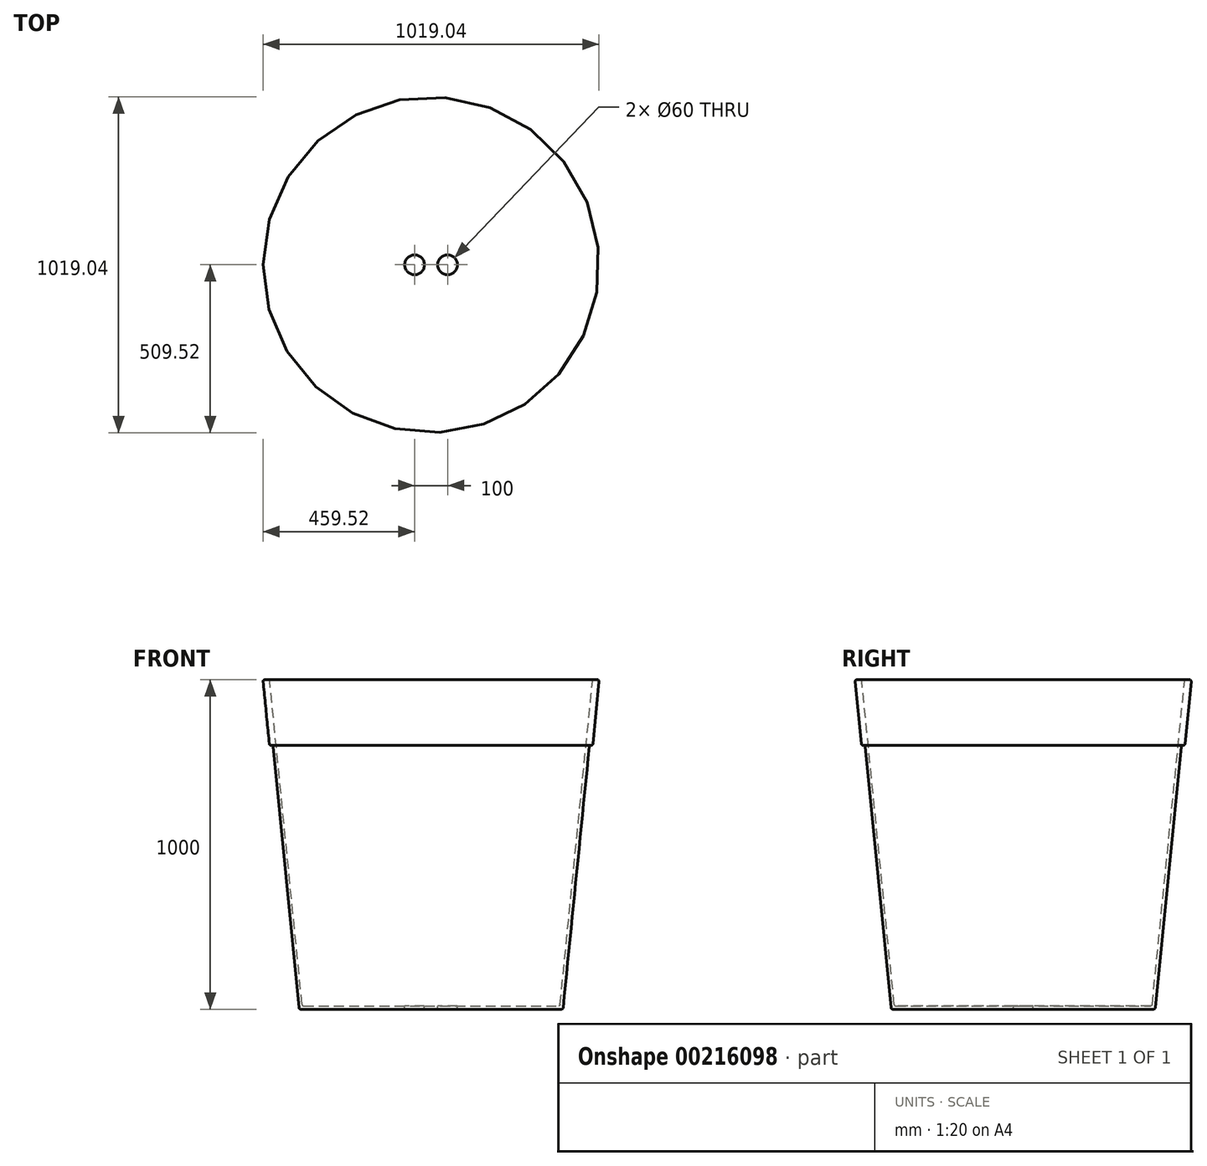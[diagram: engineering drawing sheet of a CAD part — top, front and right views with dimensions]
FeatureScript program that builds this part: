
annotation { "Feature Type Name" : "Feature", "Feature Type Description" : "" }
export const myFeature = defineFeature(function(context is Context, id is Id, definition is map)
    precondition{}
    {
        {
            var Q0;
            Q0=qCreatedBy(makeId("Front.planeOp"),FACE);
            var sketch = newSketch(context, id + "F0", { "sketchPlane" : qUnion([Q0])});
            skLineSegment(sketch, "E0", {"start": v(-400, 0) * mm, "end": v(-500, 1000) * mm});
            skLineSegment(sketch, "E1", {"start": v(-400, 0) * mm, "end": v(0, 0) * mm});
            skLineSegment(sketch, "E2", {"start": v(0, 0) * mm, "end": v(0, 10) * mm});
            skLineSegment(sketch, "E3", {"start": v(0, 10) * mm, "end": v(-390.95, 10) * mm});
            skLineSegment(sketch, "E4", {"start": v(-390.95, 10) * mm, "end": v(-489.95, 1000) * mm});
            skLineSegment(sketch, "E5", {"start": v(-489.95, 1000) * mm, "end": v(-500, 1000) * mm});
            skLineSegment(sketch, "E6", {"start": v(-500, 1000) * mm, "end": v(-510.05, 1000) * mm});
            skLineSegment(sketch, "E7", {"start": v(-510.05, 1000) * mm, "end": v(-490.15, 801) * mm});
            skLineSegment(sketch, "E8", {"start": v(-490.15, 801) * mm, "end": v(-480.1, 801) * mm});
            skLineSegment(sketch, "E9", {"start": v(0, 0) * mm, "end": v(0, 1027.65) * mm, "construction": true});
            skSolve(sketch);
        }
        {
            var Q0;
            Q0 = qSketchRegion(id + "F0", true);
            var Q1;
            Q1=sQuery(id+"F0.wireOp",EDGE,"E9");
            revolve(context, id + "F1", {"entities" : qUnion([Q0]), "axis" : qUnion([Q1]), "revolveType" : RevolveType.FULL});
        }
        {
            var Q0;
            Q0=makeQuery(id+"F1.opRevolve","SWEPT_EDGE",EDGE,{"disambiguationData":[OSD([sQuery(id+"F0.wireOp",EDGE,"E4"),sQuery(id+"F0.wireOp",EDGE,"E5")])]});
            var Q1;
            Q1=makeQuery(id+"F1.opRevolve","SWEPT_EDGE",EDGE,{"disambiguationData":[OSD([sQuery(id+"F0.wireOp",EDGE,"E6"),sQuery(id+"F0.wireOp",EDGE,"E7")])]});
            var Q2;
            Q2=makeQuery(id+"F1.opRevolve","SWEPT_EDGE",EDGE,{"disambiguationData":[OSD([sQuery(id+"F0.wireOp",EDGE,"E3"),sQuery(id+"F0.wireOp",EDGE,"E4")])]});
            var Q3;
            Q3=makeQuery(id+"F1.opRevolve","SWEPT_EDGE",EDGE,{"disambiguationData":[OSD([sQuery(id+"F0.wireOp",EDGE,"E7"),sQuery(id+"F0.wireOp",EDGE,"E8")])]});
            var Q4;
            Q4=makeQuery(id+"F1.opRevolve","SWEPT_EDGE",EDGE,{"disambiguationData":[OSD([sQuery(id+"F0.wireOp",EDGE,"E0"),sQuery(id+"F0.wireOp",EDGE,"E1")])]});
            var Q5;
            Q5=makeQuery(id+"F1.opRevolve","SWEPT_EDGE",EDGE,{"disambiguationData":[OSD([sQuery(id+"F0.wireOp",EDGE,"E0"),sQuery(id+"F0.wireOp",EDGE,"E8")])]});
            fillet(context, id + "F2", {"entities" : qUnion([Q0, Q1, Q2, Q3, Q4, Q5]), "radius" : 5 * mm, "tangentPropagation" : true, "allowEdgeOverflow" : false});
        }
        {
            var Q0;
            Q0=makeQuery(id+"F1.opRevolve","SWEPT_FACE",FACE,{"disambiguationData":[OSD([sQuery(id+"F0.wireOp",EDGE,"E3")])]});
            var sketch = newSketch(context, id + "F3", { "sketchPlane" : qUnion([Q0])});
            skCircle(sketch, "E10", {"center": v(-50, 0) * mm, "radius": 30 * mm});
            skCircle(sketch, "E11.MirrorC", {"center": v(50, 0) * mm, "radius": 30 * mm});
            skSolve(sketch);
        }
        {
            var Q0;
            Q0 = qSketchRegion(id + "F3", true);
            extrude(context, id + "F4", {"entities" : qUnion([Q0]), "operationType" : NewBodyOperationType.REMOVE, "endBound" : BoundingType.THROUGH_ALL, "oppositeDirection" : true, "depth" : 25 * mm});
        }
    });
